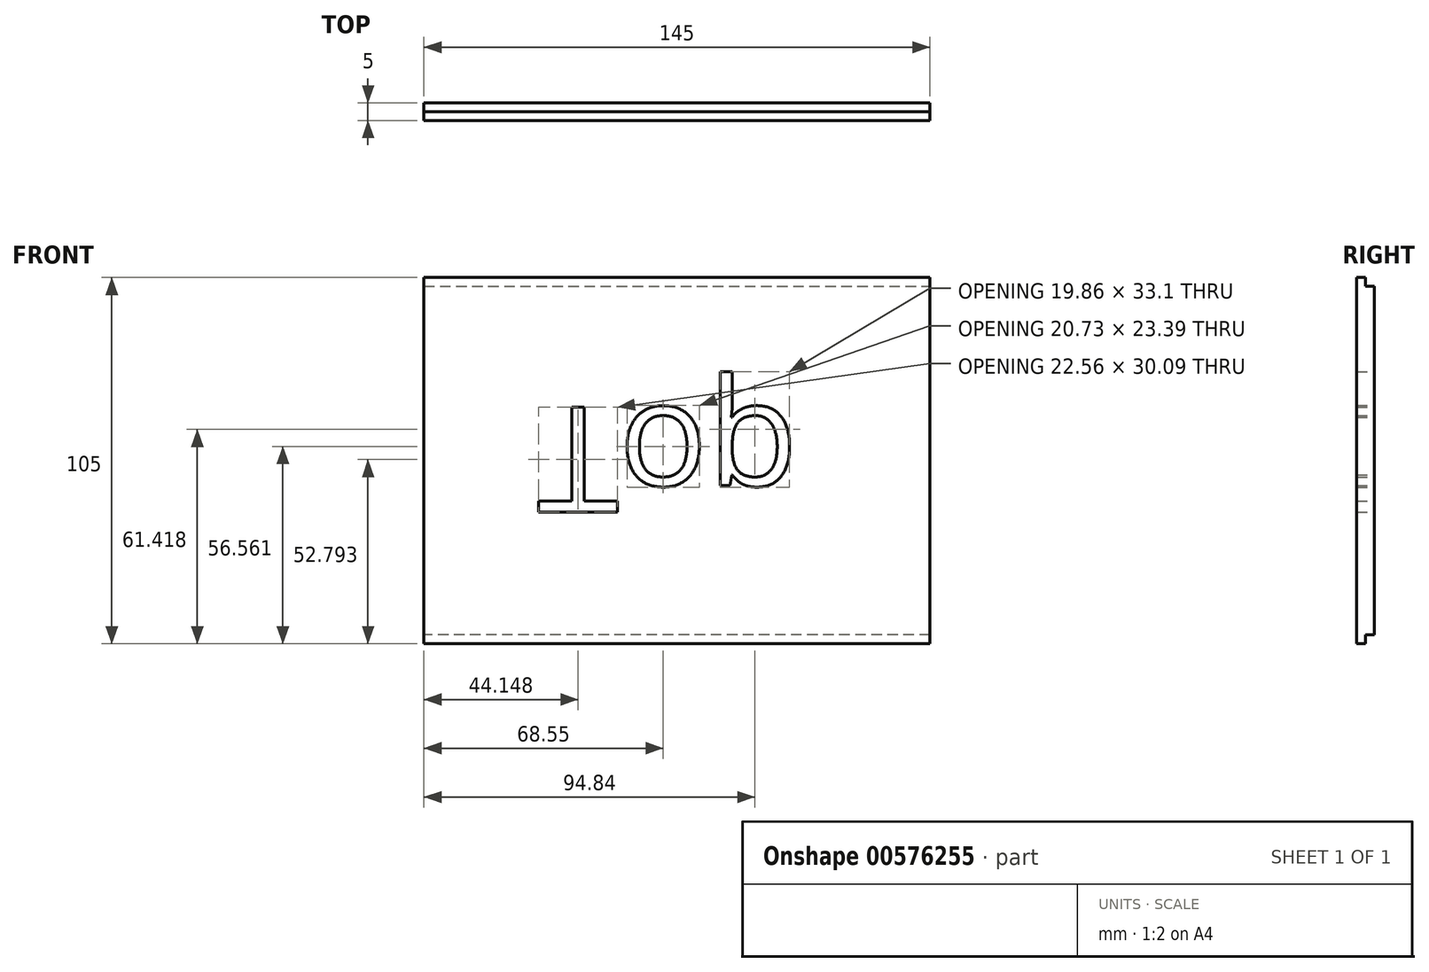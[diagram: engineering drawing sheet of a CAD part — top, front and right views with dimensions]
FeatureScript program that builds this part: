
annotation { "Feature Type Name" : "Feature", "Feature Type Description" : "" }
export const myFeature = defineFeature(function(context is Context, id is Id, definition is map)
    precondition{}
    {
        {
            var Q0;
            Q0=qCreatedBy(makeId("Front.planeOp"),FACE);
            var sketch = newSketch(context, id + "F0", { "sketchPlane" : qUnion([Q0])});
            skLineSegment(sketch, "E0.bottom", {"start": v(75, -52.5) * mm, "end": v(-70, -52.5) * mm});
            skLineSegment(sketch, "E0.left", {"start": v(75, -52.5) * mm, "end": v(75, 47.5) * mm});
            skPoint(sketch, "E0.middle", {"position": v(0, 0) * mm});
            skLineSegment(sketch, "E1", {"start": v(-70, 47.5) * mm, "end": v(75, 47.5) * mm});
            skPoint(sketch, "E2.orphan", {"position": v(75, 52.5) * mm});
            skPoint(sketch, "E3.orphan", {"position": v(-75, 52.5) * mm});
            skLineSegment(sketch, "E4", {"start": v(-70, 47.5) * mm, "end": v(-70, -52.5) * mm});
            skPoint(sketch, "E0.right.start.orphan", {"position": v(-75, -52.5) * mm});
            skSolve(sketch);
        }
        {
            var Q0;
            Q0=qSketchRegion(id+"F0",true);
            extrude(context, id + "F1", {"entities" : qUnion([Q0]), "depth" : 5 * mm, "offsetDistance" : 25 * mm});
        }
        {
            var Q0;
            Q0=makeQuery(id+"F1.opExtrude","CAP_FACE",FACE,{"disambiguationData":[OSD([sQuery(id+"F0.wireOp",EDGE,"E0.bottom"),sQuery(id+"F0.wireOp",EDGE,"E0.top"),sQuery(id+"F0.wireOp",EDGE,"E0.left"),sQuery(id+"F0.wireOp",EDGE,"E0.right")])],"isStart":true});
            var sketch = newSketch(context, id + "F2", { "sketchPlane" : qUnion([Q0])});
            skText(sketch, "E5", { "text": "Top\n", "fontName": "OpenSans-Regular.ttf"});
            const initialGuessF2  = {"E5": [0.0375, 0.01284, -1, 0, 0.03035]};
            skSetInitialGuess(sketch, initialGuessF2);
            skSolve(sketch);
        }
        {
            var Q0;
            Q0 = qSketchRegion(id + "F2", true);
            extrude(context, id + "F3", {"entities" : qUnion([Q0]), "operationType" : NewBodyOperationType.REMOVE, "oppositeDirection" : true, "depth" : 5 * mm, "offsetDistance" : 25 * mm});
        }
        {
            var Q0;
            Q0=makeQuery(id+"F1.opExtrude","SWEPT_FACE",FACE,{"disambiguationData":[OSD([sQuery(id+"F0.wireOp",EDGE,"E0.bottom")])]});
            var sketch = newSketch(context, id + "F4", { "sketchPlane" : qUnion([Q0])});
            skLineSegment(sketch, "E6", {"start": v(75, 5) * mm, "end": v(75, 2.5) * mm});
            skLineSegment(sketch, "E7", {"start": v(75, 2.5) * mm, "end": v(75, 2.5) * mm});
            skLineSegment(sketch, "E8", {"start": v(75, 2.5) * mm, "end": v(-70, 2.5) * mm});
            skSolve(sketch);
        }
        {
            var Q0;
            Q0=makeQuery(id+"F4.imprint","IMPRINT",FACE,{"disambiguationData":[TD([[makeQuery(id+"F4.imprint","IMPRINT",EDGE,{"derivedFrom":sQuery(id+"F4.wireOp",EDGE,"E6")}),-1.0]])]});
            extrude(context, id + "F5", {"entities" : qUnion([Q0]), "operationType" : NewBodyOperationType.ADD, "depth" : 2.5 * mm, "offsetDistance" : 25 * mm});
        }
        {
            var Q0;
            Q0=makeQuery(id+"F1.opExtrude","SWEPT_FACE",FACE,{"disambiguationData":[OSD([sQuery(id+"F0.wireOp",EDGE,"E1")])]});
            var sketch = newSketch(context, id + "F6", { "sketchPlane" : qUnion([Q0])});
            skLineSegment(sketch, "E9", {"start": v(75, -2.5) * mm, "end": v(75, -2.5) * mm});
            skLineSegment(sketch, "E10", {"start": v(75, -2.5) * mm, "end": v(-70, -2.5) * mm});
            skSolve(sketch);
        }
        {
            var Q0;
            Q0=makeQuery(id+"F4.imprint","IMPRINT",FACE,{"disambiguationData":[TD([[makeQuery(id+"F4.imprint","IMPRINT",EDGE,{"derivedFrom":sQuery(id+"F4.wireOp",EDGE,"E6")}),-1.0]])]});
            extrude(context, id + "F7", {"entities" : qUnion([Q0]), "operationType" : NewBodyOperationType.ADD, "depth" : 2.5 * mm, "offsetDistance" : 25 * mm});
        }
        {
            var Q0;
            {var subQ0=sQuery(id+"F6.wireOp",EDGE,"E10");Q0=makeQuery(id+"F6.imprint","IMPRINT",FACE,{"disambiguationData":[TD([[makeQuery(id+"F6.imprint","IMPRINT",EDGE,{"derivedFrom":subQ0}),1.0]])]});}
            extrude(context, id + "F8", {"entities" : qUnion([Q0]), "operationType" : NewBodyOperationType.ADD, "depth" : 2.5 * mm, "offsetDistance" : 25 * mm});
        }
    });
